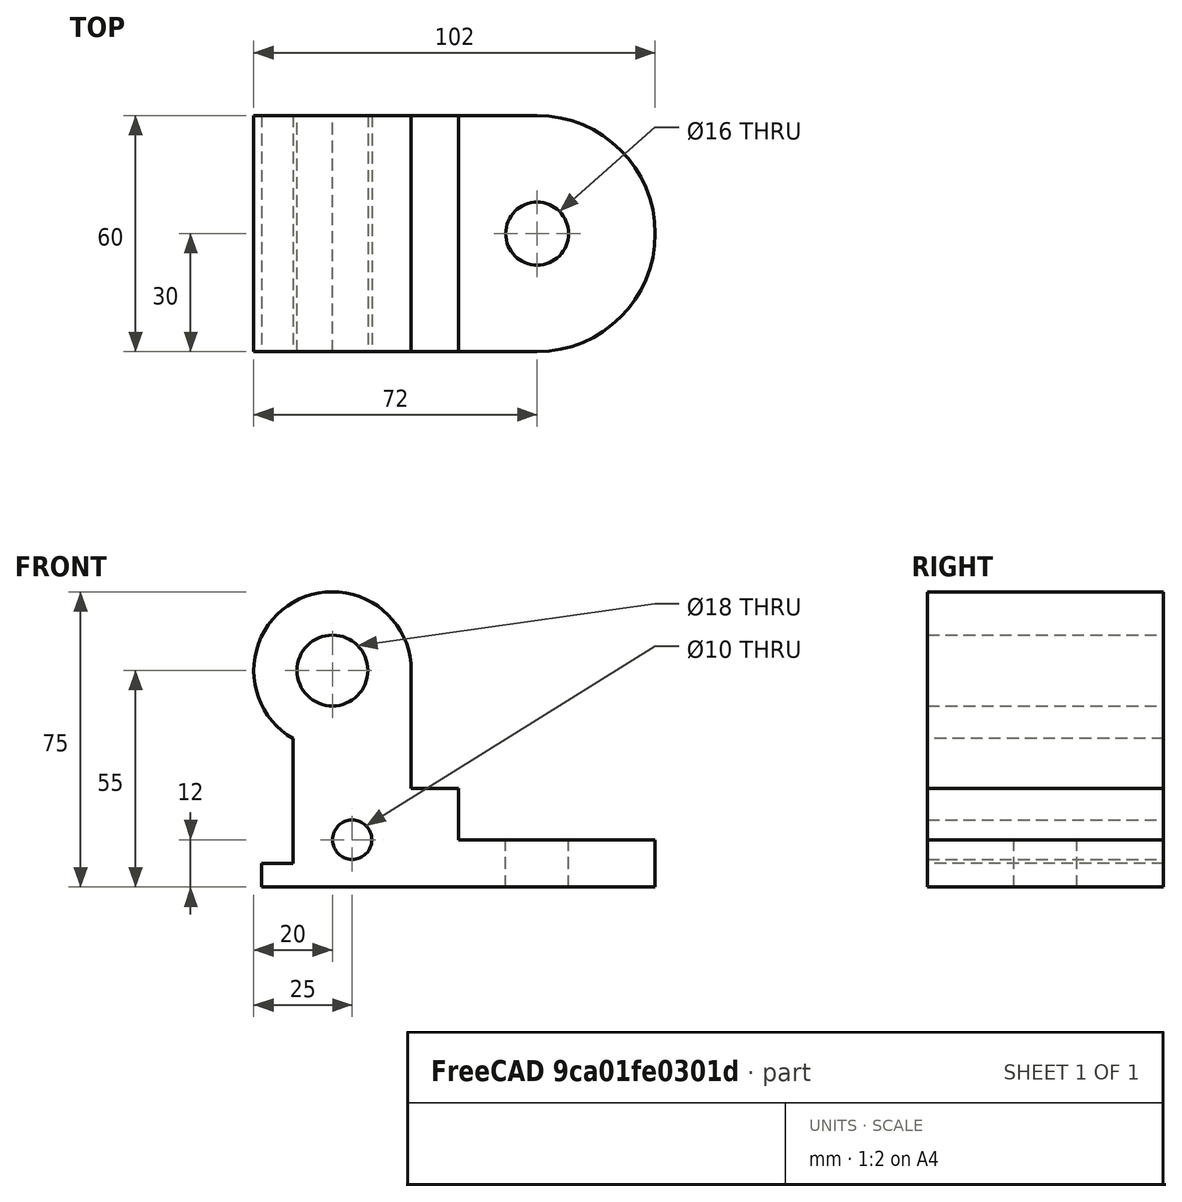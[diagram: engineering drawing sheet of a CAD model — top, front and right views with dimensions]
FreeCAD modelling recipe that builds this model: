
FCSTD DOCUMENT  (FreeCAD 0.14R3702 (Git))
Label: ejer9
License: CC-BY 3.0
LicenseURL: http://creativecommons.org/licenses/by/3.0/
objects: Part::Cylinder×2, Sketcher::SketchObject×1, PartDesign::Pad×1, Part::MultiFuse×1, Part::Cut×1
note: 7 computed .brp shape members not serialized (recipe doc carries the construction recipe); baked Part::Feature solids carry a one-line shape summary decoded from their .brp

FEATURE [Part::Cylinder] Cylinder  label="Cilindro"
  Angle = 360
  Height = 12
  Placement = pos=(52,0,0) rot=(0,0,1;0rad)
  Radius = 30
FEATURE [Part::Cylinder] Cylinder001  label="Cilindro001"
  Angle = 360
  Height = 16
  Placement = pos=(52,0,-4) rot=(0,0,1;0rad)
  Radius = 8
FEATURE [Sketcher::SketchObject] Sketch
  Placement = pos=(0,0,0) rot=(-1,0,0;4.71239rad)
  Support = -> Cut [Face10]
  sketch-geometry (12):
    g0: LineSegment StartX=-18 StartY=0 StartZ=0 EndX=52 EndY=0 EndZ=0
    g1: LineSegment StartX=52 StartY=0 StartZ=0 EndX=52 EndY=12 EndZ=0
    g2: LineSegment StartX=52 StartY=12 StartZ=0 EndX=32 EndY=12 EndZ=0
    g3: LineSegment StartX=32 StartY=12 StartZ=0 EndX=32 EndY=25 EndZ=0
    g4: LineSegment StartX=32 StartY=25 StartZ=0 EndX=20 EndY=25 EndZ=0
    g5: LineSegment StartX=20 StartY=25 StartZ=0 EndX=20 EndY=55 EndZ=0
    g6: LineSegment StartX=-18 StartY=0 StartZ=0 EndX=-18 EndY=6 EndZ=0
    g7: LineSegment StartX=-18 StartY=6 StartZ=0 EndX=-10 EndY=6 EndZ=0
    g8: LineSegment StartX=-10 StartY=6 StartZ=0 EndX=-10 EndY=37.6795 EndZ=0
    g9: ArcOfCircle CenterX=0 CenterY=55 CenterZ=0 NormalX=0 NormalY=0 NormalZ=1 Radius=20 StartAngle=2.4493e-06 EndAngle=4.18879
    g10: Circle CenterX=0 CenterY=55 CenterZ=0 NormalX=0 NormalY=0 NormalZ=1 Radius=9
    g11: Circle CenterX=5 CenterY=12 CenterZ=0 NormalX=0 NormalY=0 NormalZ=1 Radius=5
  constraints (36):
    c: Horizontal(g0)
    c: Coincident(g0,g1)
    c: Vertical(g1)
    c: Coincident(g1,g2)
    c: Horizontal(g2)
    c: Coincident(g2,g3)
    c: Vertical(g3)
    c: Coincident(g3,g4)
    c: Horizontal(g4)
    c: Coincident(g4,g5)
    c: Vertical(g5)
    c: Coincident(g0,g6)
    c: Coincident(g6,g7)
    c: Coincident(g7,g8)
    c: DistanceY(g-1,g9) = 55
    c: Radius(g9) = 20
    c: Coincident(g10,g9)
    c: Radius(g10) = 9
    c: Vertical(g6)
    c: DistanceX(g0) = 70
    c: DistanceY(g1) = 12
    c: DistanceY(g6) = 6
    c: DistanceX(g7) = 8
    c: Horizontal(g7)
    c: Vertical(g8)
    c: DistanceX(g2) = -20
    c: DistanceY(g3) = 13
    c: DistanceX(g4) = -12
    c: PointOnObject(g0,g-1)
    c: PointOnObject(g9,g-2)
    c: DistanceX(g11,g4) = 15
    c: DistanceY(g11,g0) = -12
    c: Radius(g11) = 5
    c: Tangent(g5,g9)
    c: Coincident(g9,g5)
    c: Coincident(g9,g8)
FEATURE [PartDesign::Pad] Pad
  Length = 60
  Length2 = 100
  Midplane = true
  Placement = pos=(0,0,0) rot=(-1,0,0;4.71239rad)
  Sketch = -> Sketch
  Type = 0
FEATURE [Part::MultiFuse] Fusion
  Shapes = -> [Pad,Cylinder]
FEATURE [Part::Cut] Cut
  Base = -> Fusion
  Tool = -> Cylinder001
